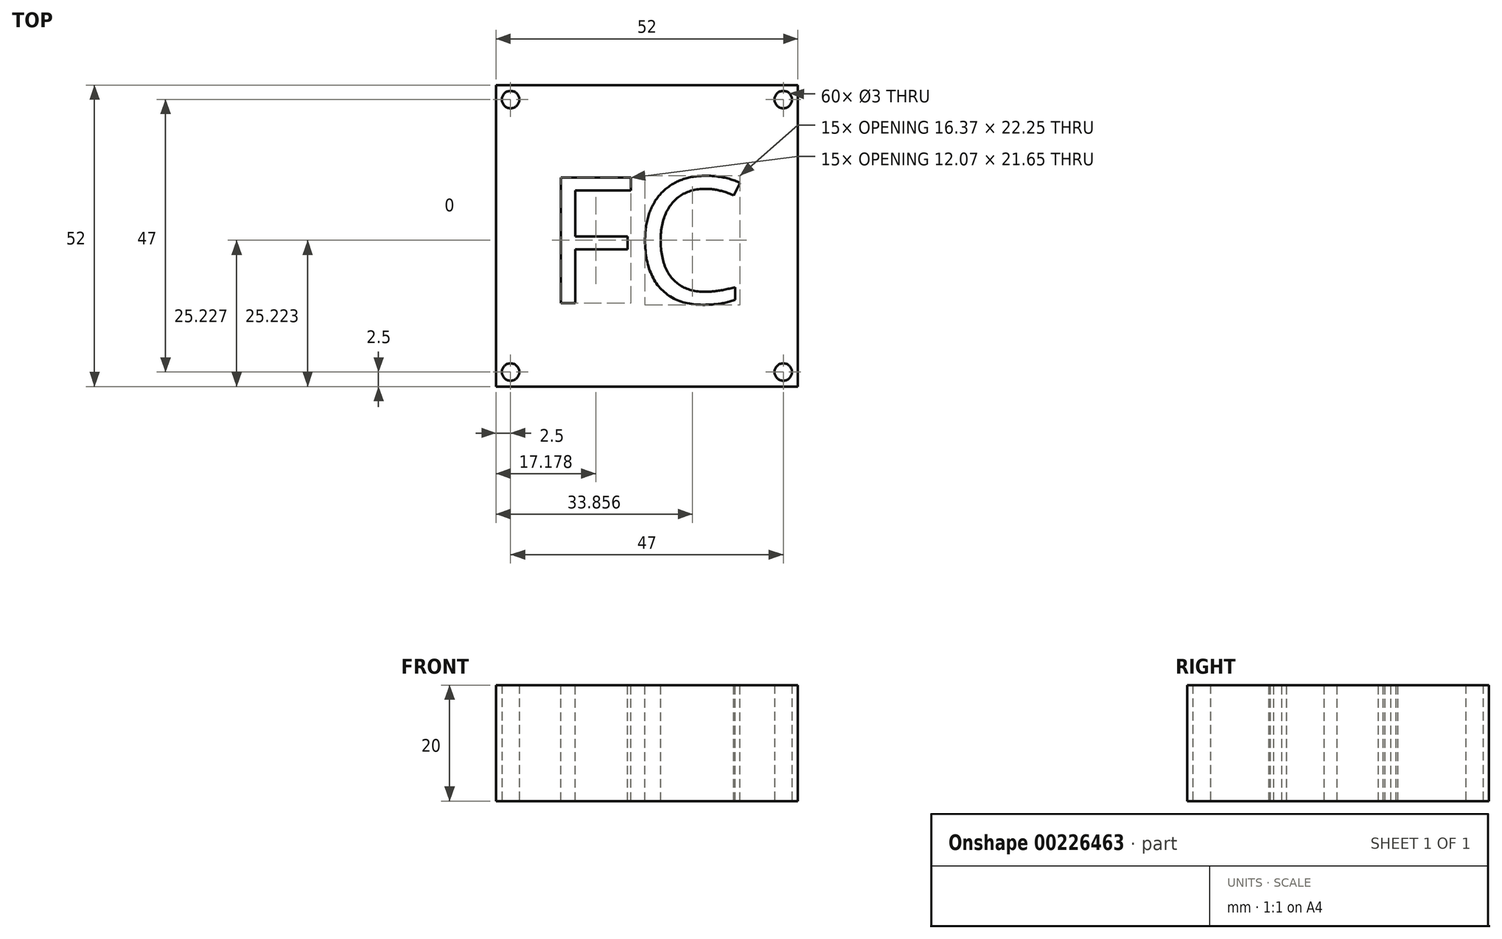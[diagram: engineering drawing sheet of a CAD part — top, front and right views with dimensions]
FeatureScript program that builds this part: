
annotation { "Feature Type Name" : "Feature", "Feature Type Description" : "" }
export const myFeature = defineFeature(function(context is Context, id is Id, definition is map)
    precondition{}
    {
        {
            var Q0;
            Q0=qCreatedBy(makeId("Top.planeOp"),FACE);
            var sketch = newSketch(context, id + "F0", { "sketchPlane" : qUnion([Q0])});
            skLineSegment(sketch, "E0.bottom", {"start": v(26, 26) * mm, "end": v(-26, 26) * mm});
            skLineSegment(sketch, "E0.top", {"start": v(26, -26) * mm, "end": v(-26, -26) * mm});
            skLineSegment(sketch, "E0.left", {"start": v(26, 26) * mm, "end": v(26, -26) * mm});
            skLineSegment(sketch, "E0.right", {"start": v(-26, 26) * mm, "end": v(-26, -26) * mm});
            skPoint(sketch, "E0.middle", {"position": v(0, 0) * mm});
            skLineSegment(sketch, "E1.bottom", {"start": v(21, 21) * mm, "end": v(-21, 21) * mm});
            skLineSegment(sketch, "E1.top", {"start": v(21, -21) * mm, "end": v(-21, -21) * mm});
            skLineSegment(sketch, "E1.left", {"start": v(21, 21) * mm, "end": v(21, -21) * mm});
            skLineSegment(sketch, "E1.right", {"start": v(-21, 21) * mm, "end": v(-21, -21) * mm});
            skLineSegment(sketch, "E2", {"start": v(-26, 26) * mm, "end": v(-21, 21) * mm});
            skLineSegment(sketch, "E3", {"start": v(-21, -21) * mm, "end": v(-26, -26) * mm});
            skLineSegment(sketch, "E4", {"start": v(21, -21) * mm, "end": v(26, -26) * mm});
            skLineSegment(sketch, "E5", {"start": v(26, 26) * mm, "end": v(21, 21) * mm});
            skCircle(sketch, "E6", {"center": v(-23.5, 23.5) * mm, "radius": 1.5 * mm});
            skCircle(sketch, "E7", {"center": v(23.5, 23.5) * mm, "radius": 1.5 * mm});
            skCircle(sketch, "E8", {"center": v(23.5, -23.5) * mm, "radius": 1.5 * mm});
            skCircle(sketch, "E9", {"center": v(-23.5, -23.5) * mm, "radius": 1.5 * mm});
            skSolve(sketch);
        }
        {
            var Q0;
            Q0=makeQuery(id+"F0.imprint","IMPRINT",FACE,{"disambiguationData":[TD([[makeQuery(id+"F0.imprint","IMPRINT",EDGE,{"derivedFrom":sQuery(id+"F0.wireOp",EDGE,"E0.bottom")}),1.0]])]});
            var Q1;
            {var subQ4=sQuery(id+"F0.wireOp",EDGE,"E0.right");Q1=makeQuery(id+"F0.imprint","IMPRINT",FACE,{"disambiguationData":[TD([[makeQuery(id+"F0.imprint","IMPRINT",EDGE,{"derivedFrom":subQ4}),1.0]])]});}
            var Q2;
            Q2=makeQuery(id+"F0.imprint","IMPRINT",FACE,{"disambiguationData":[TD([[makeQuery(id+"F0.imprint","IMPRINT",EDGE,{"derivedFrom":sQuery(id+"F0.wireOp",EDGE,"E1.bottom")}),1.0]])]});
            var Q3;
            {var subQ5=sQuery(id+"F0.wireOp",EDGE,"E0.left");Q3=makeQuery(id+"F0.imprint","IMPRINT",FACE,{"disambiguationData":[TD([[makeQuery(id+"F0.imprint","IMPRINT",EDGE,{"derivedFrom":subQ5}),-1.0]])]});}
            var Q4;
            {var subQ1=sQuery(id+"F0.wireOp",EDGE,"E0.top");Q4=makeQuery(id+"F0.imprint","IMPRINT",FACE,{"disambiguationData":[TD([[makeQuery(id+"F0.imprint","IMPRINT",EDGE,{"derivedFrom":subQ1}),-1.0]])]});}
            extrude(context, id + "F1", {"entities" : qUnion([Q0, Q1, Q2, Q3, Q4]), "depth" : 20 * mm});
        }
        {
            var Q0;
            Q0=makeQuery(id+"F1.opExtrude","CAP_FACE",FACE,{"disambiguationData":[OSD([sQuery(id+"F0.wireOp",EDGE,"E0.bottom"),sQuery(id+"F0.wireOp",EDGE,"E0.top"),sQuery(id+"F0.wireOp",EDGE,"E0.left"),sQuery(id+"F0.wireOp",EDGE,"E0.right")])],"isStart":false});
            var sketch = newSketch(context, id + "F2", { "sketchPlane" : qUnion([Q0])});
            skText(sketch, "E10", { "text": "FC", "fontName": "OpenSans-Regular.ttf"});
            const initialGuessF2  = {"E10": [-0.01783, -0.0116, 1, 0, 0.02183]};
            skSetInitialGuess(sketch, initialGuessF2);
            skSolve(sketch);
        }
        {
            var Q0;
            Q0 = qSketchRegion(id + "F2", true);
            extrude(context, id + "F3", {"entities" : qUnion([Q0]), "operationType" : NewBodyOperationType.REMOVE, "oppositeDirection" : true, "depth" : 25.4 * mm});
        }
    });
